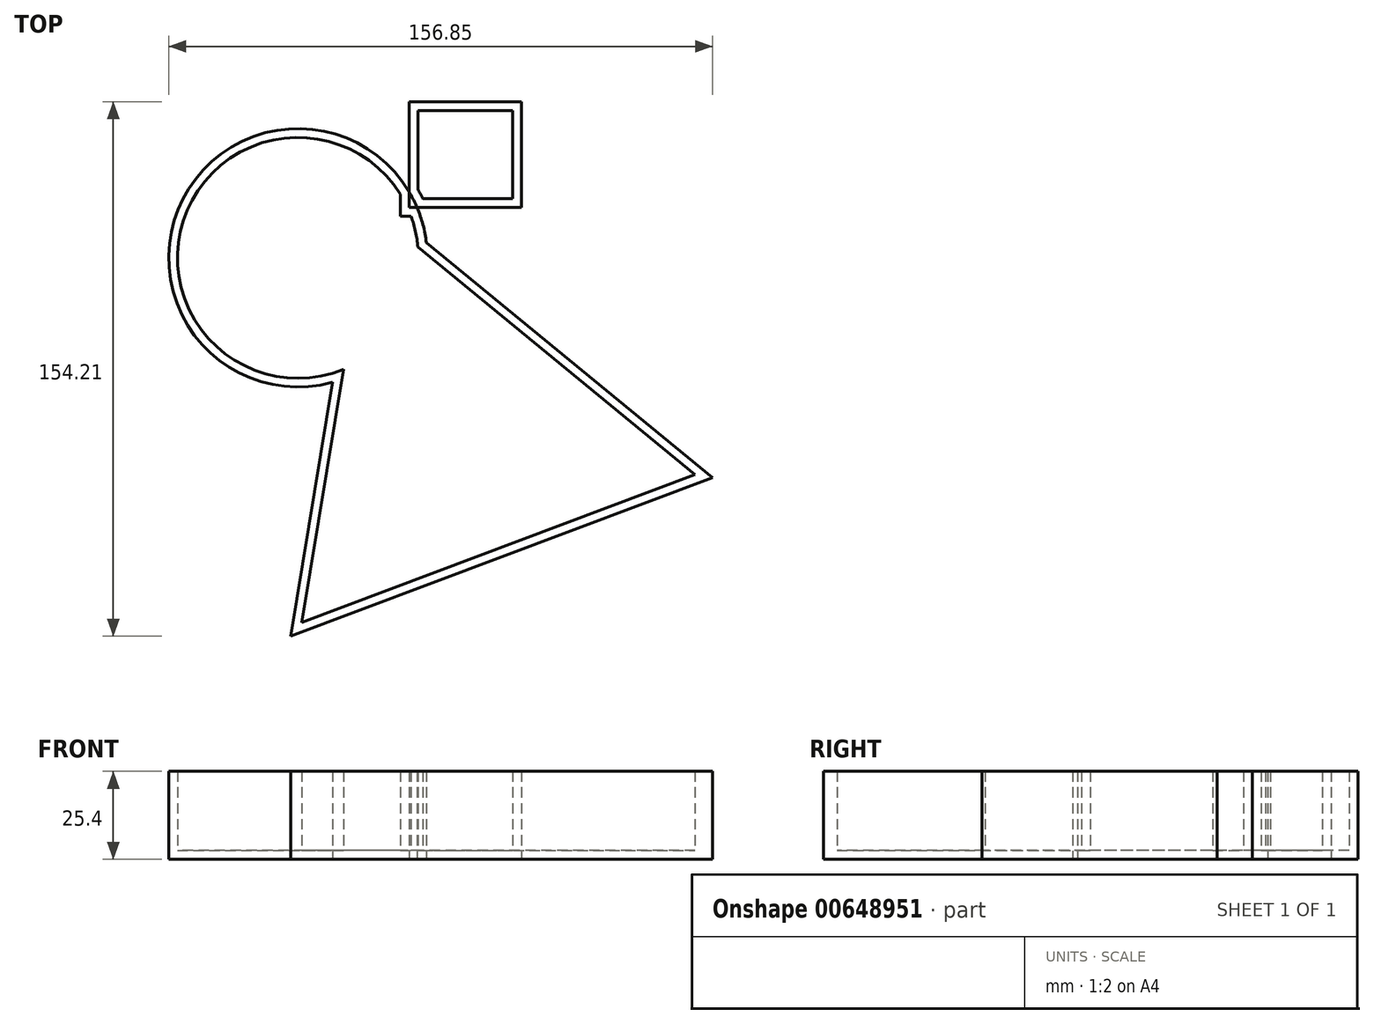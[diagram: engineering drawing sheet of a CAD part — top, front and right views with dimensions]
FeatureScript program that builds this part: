
annotation { "Feature Type Name" : "Feature", "Feature Type Description" : "" }
export const myFeature = defineFeature(function(context is Context, id is Id, definition is map)
    precondition{}
    {
        {
            var Q0;
            Q0=qCreatedBy(makeId("Top.planeOp"),FACE);
            var sketch = newSketch(context, id + "F0", { "sketchPlane" : qUnion([Q0])});
            skCircle(sketch, "E0", {"center": v(-11.76, 0) * mm, "radius": 37.29 * mm});
            skLineSegment(sketch, "E1.bottom", {"start": v(20.3, 45.04) * mm, "end": v(52.68, 45.04) * mm});
            skLineSegment(sketch, "E1.top", {"start": v(20.3, 14.5) * mm, "end": v(52.68, 14.5) * mm});
            skLineSegment(sketch, "E1.left", {"start": v(20.3, 45.04) * mm, "end": v(20.3, 14.5) * mm});
            skLineSegment(sketch, "E1.right", {"start": v(52.68, 45.04) * mm, "end": v(52.68, 14.5) * mm});
            skCircle(sketch, "E2.cCircle", {"center": v(33.74, -51.15) * mm, "radius": 37.54 * mm, "construction": true});
            skLineSegment(sketch, "E2.0", {"start": v(7.32, 19.12) * mm, "end": v(107.81, -63.4) * mm});
            skLineSegment(sketch, "E2.1", {"start": v(107.81, -63.4) * mm, "end": v(-13.9, -109.17) * mm});
            skLineSegment(sketch, "E2.2", {"start": v(-13.9, -109.17) * mm, "end": v(7.32, 19.12) * mm});
            skPoint(sketch, "E2.0.midPoint", {"position": v(57.56, -22.14) * mm});
            skSolve(sketch);
        }
        {
            var Q0;
            {var subQ1=sQuery(id+"F0.wireOp",EDGE,"E1.bottom");Q0=makeQuery(id+"F0.imprint","IMPRINT",FACE,{"disambiguationData":[TD([[makeQuery(id+"F0.imprint","IMPRINT",EDGE,{"derivedFrom":subQ1}),-1.0]])]});}
            var Q1;
            {var subQ1=sQuery(id+"F0.wireOp",EDGE,"E1.top");var subQ3=sQuery(id+"F0.wireOp",EDGE,"E0");var subQ7=makeQuery(id+"F0.imprint","INTERSECT",VERTEX,{"derivedFrom":[subQ3,subQ1]});Q1=makeQuery(id+"F0.imprint","IMPRINT",FACE,{"disambiguationData":[TD([[makeQuery(id+"F0.imprint","IMPRINT",EDGE,{"disambiguationData":[TD([[subQ7,1.0]])],"derivedFrom":subQ3}),1.0]])]});}
            var Q2;
            {var subQ5=sQuery(id+"F0.wireOp",EDGE,"E2.1");Q2=makeQuery(id+"F0.imprint","IMPRINT",FACE,{"disambiguationData":[TD([[makeQuery(id+"F0.imprint","IMPRINT",EDGE,{"derivedFrom":subQ5}),-1.0]])]});}
            var Q3;
            {var subQ0=sQuery(id+"F0.wireOp",EDGE,"E2.0");var subQ1=sQuery(id+"F0.wireOp",EDGE,"E0");var subQ2=makeQuery(id+"F0.imprint","INTERSECT",VERTEX,{"derivedFrom":[subQ1,subQ0]});Q3=makeQuery(id+"F0.imprint","IMPRINT",FACE,{"disambiguationData":[TD([[makeQuery(id+"F0.imprint","IMPRINT",EDGE,{"disambiguationData":[TD([[subQ2,1.0]])],"derivedFrom":subQ1}),1.0]])]});}
            extrude(context, id + "F1", {"entities" : qUnion([Q0, Q1, Q2, Q3]), "depth" : 25.4 * mm, "offsetDistance" : 25.4 * mm});
        }
        {
            var Q0;
            Q0=makeQuery(id+"F1.opExtrude","CAP_FACE",FACE,{"disambiguationData":[OSD([sQuery(id+"F0.wireOp",EDGE,"E0"),sQuery(id+"F0.wireOp",EDGE,"E1.top"),sQuery(id+"F0.wireOp",EDGE,"E1.left"),sQuery(id+"F0.wireOp",EDGE,"E2.0"),sQuery(id+"F0.wireOp",EDGE,"E2.1"),sQuery(id+"F0.wireOp",EDGE,"E2.2")])],"isStart":false});
            var Q1;
            Q1=makeQuery(id+"F1.opExtrude","CAP_FACE",FACE,{"disambiguationData":[OSD([sQuery(id+"F0.wireOp",EDGE,"E0"),sQuery(id+"F0.wireOp",EDGE,"E1.bottom"),sQuery(id+"F0.wireOp",EDGE,"E1.top"),sQuery(id+"F0.wireOp",EDGE,"E1.left"),sQuery(id+"F0.wireOp",EDGE,"E1.right")])],"isStart":false});
            shell(context, id + "F2", {"entities" : qUnion([Q0, Q1]), "thickness" : 2.54 * mm});
        }
    });
